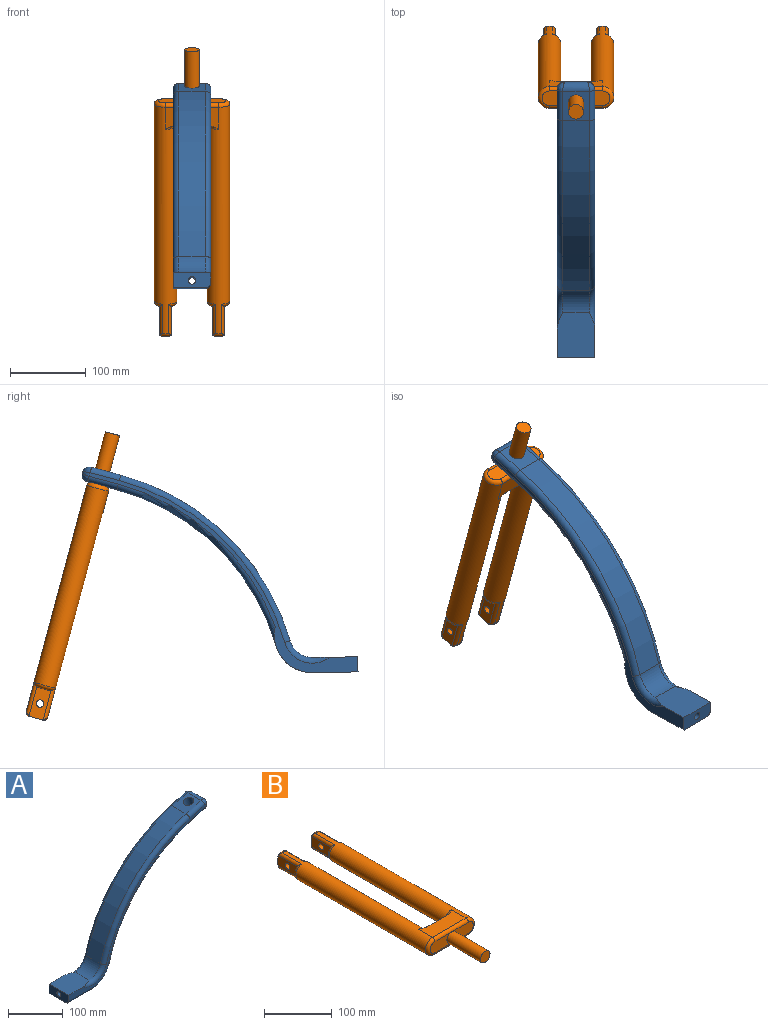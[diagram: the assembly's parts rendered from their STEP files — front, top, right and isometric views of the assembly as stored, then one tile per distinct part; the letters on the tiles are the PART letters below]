
ASSEMBLY  parts=2 mates=1
PART A: 35 faces, bbox 363.3x52x297.2 mm
  f0: cylinder r=50mm len=62.38mm, axis (0,1,0), area 2759mm2, adj f1,f30,f31,f32,f33,f34
  f1: cylinder r=5mm len=95.71mm, axis (-1,0,0), area 2808.2mm2, adj f0,f2
  f2: plane 50x20mm, normal (-1,0,0), area 909.4mm2, adj f1,f3,f28,f29,f31,f32
  f3: plane 61.97x51.97mm, normal (0,0,1), area 2871.7mm2, adj f2,f4,f26,f27,f28,f31
  f4: torus R=37.5mm, axis (0,-1,0), area 639.4mm2, adj f3,f5,f27,f28
  f5: torus R=312.5mm, axis (0,-1,0), area 3830.1mm2, adj f4,f6,f25,f28
  f6: cylinder r=320mm len=222.99mm, axis (0,1,0), area 11476.5mm2, adj f5,f7,f24,f27
  f7: torus R=312.5mm, axis (0,-1,0), area 3830.1mm2, adj f6,f8,f26,f31
  f8: cylinder r=7.5mm len=40.52mm, axis (-0.96,0,-0.27), area 471.2mm2, adj f7,f9,f24,f31
  f9: bspline ~14.48x10mm, area 81.9mm2, adj f8,f10,f23
  f10: cylinder r=10mm len=35mm, axis (0,1,0), area 1029.2mm2, adj f9,f11,f13,f14,f18,f20,f21,f22
  f11: bspline ~10.77x10.7mm, area 52.8mm2, adj f10,f12,f23
  f12: cylinder r=7.5mm len=40.52mm, axis (0.96,0,0.27), area 471.2mm2, adj f11,f14,f30,f31
  f13: bspline ~7.89x7.3mm, area 9.9mm2, adj f10,f23
  f14: plane 38.46x35mm, normal (0.27,0,-0.96), area 1085.8mm2, adj f10,f12,f15,f17,f34
  f15: cylinder r=7.5mm len=40.52mm, axis (-0.96,0,-0.27), area 471.2mm2, adj f14,f16,f18,f28
  f16: torus R=307.5mm, axis (0,-1,0), area 3654.8mm2, adj f15,f28,f33,f34
  f17: cylinder r=10mm len=24.72mm, axis (-0.27,0,0.96), area 1256.6mm2, adj f14,f24
  f18: bspline ~10.77x10.7mm, area 52.8mm2, adj f10,f15,f19
  f19: cylinder r=10mm len=10.99mm, axis (0.27,0,-0.96), area 39.3mm2, adj f18,f20,f21,f22,f28
  f20: bspline ~7.89x7.3mm, area 9.9mm2, adj f10,f19
  f21: bspline ~7.3x6.15mm, area 9.9mm2, adj f10,f19
  f22: bspline ~12.62x8.48mm, area 52.8mm2, adj f10,f19,f25
  f23: cylinder r=10mm len=10.99mm, axis (-0.27,0,0.96), area 39.3mm2, adj f9,f11,f13,f31
  f24: plane 38.46x35mm, normal (-0.27,0,0.96), area 1085.8mm2, adj f6,f8,f10,f17,f25
  f25: cylinder r=7.5mm len=40.52mm, axis (0.96,0,0.27), area 471.2mm2, adj f5,f22,f24,f28
  f26: torus R=37.5mm, axis (0,-1,0), area 639.4mm2, adj f3,f7,f27,f31
  f27: cylinder r=30mm len=35mm, axis (0,1,0), area 1392.9mm2, adj f3,f4,f6,f26
  f28: plane 351.71x262mm, normal (0,-1,0), area 2687.2mm2, adj f2,f3,f4,f5,f15,f16,f19,f25
  f29: cylinder r=7.5mm len=60mm, axis (-1,0,0), area 706.9mm2, adj f2,f28,f32,f33
  f30: torus R=307.5mm, axis (0,-1,0), area 3514.2mm2, adj f0,f12,f31,f34
  f31: plane 351.71x269.5mm, normal (0,1,0), area 3714.7mm2, adj f0,f2,f3,f7,f8,f12,f23,f26
  f32: plane 60x42.5mm, normal (0,0,-1), area 2550mm2, adj f0,f2,f29,f31
  f33: torus R=42.5mm, axis (0,-1,0), area 733.8mm2, adj f0,f16,f28,f29
  f34: cylinder r=300mm len=209.05mm, axis (0,1,0), area 10759.2mm2, adj f0,f14,f16,f30
PART B: 43 faces, bbox 102.5x390x51 mm
  f0: plane 45x20mm, normal (0,-1,0), area 700mm2, adj f19,f22,f23,f24
  f1: plane 13.23x2.5mm, normal (0,1,0), area 22.7mm2, adj f15,f41
  f2: plane 13.23x2.5mm, normal (0,1,0), area 22.7mm2, adj f11,f32
  f3: cylinder r=15mm len=310mm, axis (0,1,0), area 24639.6mm2, adj f4,f6,f24,f34,f35,f36,f37,f38
  f4: plane 70x30mm, normal (0,0,-1), area 1799.2mm2, adj f3,f5,f8,f23,f33,f42
  f5: cylinder r=15mm len=310mm, axis (0,1,0), area 24639.6mm2, adj f4,f6,f21,f25,f26,f27,f28,f29
  f6: plane 70x30mm, normal (0,0,1), area 1799.2mm2, adj f3,f5,f8,f22,f33,f42
  f7: plane 45x20mm, normal (0,-1,0), area 700mm2, adj f19,f21,f22,f23
  f8: plane 43.54x30mm, normal (0,1,0), area 1024.7mm2, adj f4,f6,f33,f42
  f9: plane 13.23x2.5mm, normal (0,1,0), area 22.7mm2, adj f14,f34
  f10: plane 13.23x2.5mm, normal (0,1,0), area 22.7mm2, adj f12,f25
  f11: plane 40.53x19.37mm, normal (-1,0,0), area 696.1mm2, adj f2,f13,f18,f28,f29,f30,f31,f32
  f12: plane 40.53x19.37mm, normal (1,0,0), area 696.1mm2, adj f10,f13,f18,f25,f26,f27,f28,f29
  f13: plane 20x15mm, normal (0,1,0), area 268.8mm2, adj f11,f12,f28,f29
  f14: plane 40.53x19.37mm, normal (1,0,0), area 696.1mm2, adj f9,f16,f17,f34,f35,f36,f37,f38
  f15: plane 40.53x19.37mm, normal (-1,0,0), area 696.1mm2, adj f1,f16,f17,f37,f38,f39,f40,f41
  f16: plane 20x15mm, normal (0,1,0), area 268.8mm2, adj f14,f15,f37,f38
  f17: cylinder r=5mm len=15mm, axis (1,0,0), area 471.2mm2, adj f14,f15
  f18: cylinder r=5mm len=15mm, axis (1,0,0), area 471.2mm2, adj f11,f12
  f19: cylinder r=10mm len=70mm, axis (0,1,0), area 4398.2mm2, adj f0,f7,f20
  f20: plane 20x20mm, normal (0,-1,0), area 314.2mm2, adj f19
  f21: torus R=10mm, axis (0,-1,0), area 325.3mm2, adj f5,f7,f22,f23
  f22: cylinder r=5mm len=70mm, axis (1,0,0), area 549.8mm2, adj f0,f6,f7,f21,f24
  f23: cylinder r=5mm len=70mm, axis (-1,0,0), area 549.8mm2, adj f0,f4,f7,f21,f24
  f24: torus R=10mm, axis (0,-1,0), area 325.3mm2, adj f0,f3,f22,f23
  f25: torus R=10mm, axis (0,-1,0), area 215.4mm2, adj f5,f10,f12,f26,f27
  f26: cylinder r=5mm len=44.47mm, axis (0,1,0), area 263.6mm2, adj f5,f12,f25,f28
  f27: cylinder r=5mm len=44.47mm, axis (0,1,0), area 263.6mm2, adj f5,f12,f25,f29
  f28: torus R=10mm, axis (0,1,0), area 109.8mm2, adj f5,f11,f12,f13,f26,f30
  f29: torus R=10mm, axis (0,1,0), area 109.8mm2, adj f5,f11,f12,f13,f27,f31
  f30: cylinder r=5mm len=44.47mm, axis (0,1,0), area 263.6mm2, adj f5,f11,f28,f32
  f31: cylinder r=5mm len=44.47mm, axis (0,1,0), area 263.6mm2, adj f5,f11,f29,f32
  f32: torus R=10mm, axis (0,-1,0), area 215.4mm2, adj f2,f5,f11,f30,f31
  f33: torus R=20mm, axis (0,-1,0), area 303.6mm2, adj f4,f5,f6,f8
  f34: torus R=10mm, axis (0,-1,0), area 215.4mm2, adj f3,f9,f14,f35,f36
  f35: cylinder r=5mm len=44.47mm, axis (0,1,0), area 263.6mm2, adj f3,f14,f34,f37
  f36: cylinder r=5mm len=44.47mm, axis (0,1,0), area 263.6mm2, adj f3,f14,f34,f38
  f37: torus R=10mm, axis (0,1,0), area 109.8mm2, adj f3,f14,f15,f16,f35,f39
  f38: torus R=10mm, axis (0,1,0), area 109.8mm2, adj f3,f14,f15,f16,f36,f40
  f39: cylinder r=5mm len=44.47mm, axis (0,1,0), area 263.6mm2, adj f3,f15,f37,f41
  f40: cylinder r=5mm len=44.47mm, axis (0,1,0), area 263.6mm2, adj f3,f15,f38,f41
  f41: torus R=10mm, axis (0,-1,0), area 215.4mm2, adj f1,f3,f15,f39,f40
  f42: torus R=20mm, axis (0,-1,0), area 303.6mm2, adj f3,f4,f6,f8
PLACE A rot(axis=(-0.01,0.01,1),90deg) t=(-47.09,70.59,-29.39)mm
PLACE B rot(axis=(-1,0,0),75deg) t=(-2.09,-15.87,227.02)mm
MATE slider A.f17 <-> B.f19  axis (0,-0.26,0.97) through (-22.09,11.92,286.17)mm
